annotation { "Feature Type Name" : "Feature", "Feature Type Description" : "" }
export const myFeature = defineFeature(function(context is Context, id is Id, definition is map)
    precondition{}
    {
        {
            var Q0;
            Q0=qCreatedBy(makeId("Top.planeOp"),FACE);
            var sketch = newSketch(context, id + "F0", { "sketchPlane" : qUnion([Q0])});
            skText(sketch, "E0", { "text": "RED ROBIN", "fontName": "OpenSans-Bold.ttf"});
            const initialGuessF0  = {"E0": [-0.07626, -0.00374, 1, 0, 0.02]};
            skSetInitialGuess(sketch, initialGuessF0);
            skSolve(sketch);
        }
        {
            var Q0;
            Q0 = qSketchRegion(id + "F0", true);
            extrude(context, id + "F1", {"entities" : qUnion([Q0]), "depth" : 3 * mm, "offsetDistance" : 25 * mm});
        }
        {
            var Q0;
            Q0=qCreatedBy(makeId("Top.planeOp"),FACE);
            var sketch = newSketch(context, id + "F2", { "sketchPlane" : qUnion([Q0])});
            skEllipse(sketch, "E1", {"center": v(0, 0) * mm, "majorRadius": 100 * mm, "minorRadius": 60 * mm, "majorAxis": v(1, 0)});
            skFitSpline(sketch, "E2.0", {"points": [v(94.93, -2.57) * mm, v(95.04, 0) * mm, v(94.93, 2.57) * mm, v(94.5, 5.97) * mm, v(93.46, 10.19) * mm, v(91.36, 15.2) * mm, v(88.41, 20.14) * mm, v(84.62, 24.96) * mm, v(80.76, 28.83) * mm, v(77.26, 31.82) * mm, v(74.43, 34) * mm, v(71.4, 36.11) * mm, v(68.17, 38.15) * mm, v(64.76, 40.1) * mm, v(61.2, 41.94) * mm, v(57.49, 43.68) * mm, v(52.36, 45.84) * mm, v(45.64, 48.25) * mm, v(37.12, 50.66) * mm, v(28.24, 52.57) * mm, v(20.58, 53.73) * mm, v(14.33, 54.39) * mm, v(9.6, 54.74) * mm, v(5.61, 54.92) * mm, v(2.41, 54.99) * mm, v(0, 55) * mm, v(-2.41, 54.99) * mm, v(-5.61, 54.92) * mm, v(-9.6, 54.74) * mm, v(-14.33, 54.39) * mm, v(-20.58, 53.73) * mm, v(-28.24, 52.57) * mm, v(-37.12, 50.66) * mm, v(-45.64, 48.25) * mm, v(-52.36, 45.84) * mm, v(-57.49, 43.68) * mm, v(-61.2, 41.94) * mm, v(-64.76, 40.1) * mm, v(-68.17, 38.15) * mm, v(-71.4, 36.11) * mm, v(-74.43, 34) * mm, v(-77.26, 31.82) * mm, v(-80.76, 28.83) * mm, v(-84.62, 24.96) * mm, v(-88.41, 20.14) * mm, v(-91.36, 15.2) * mm, v(-93.46, 10.19) * mm, v(-94.5, 5.97) * mm, v(-94.93, 2.57) * mm, v(-95.04, 0) * mm, v(-94.93, -2.57) * mm, v(-94.5, -5.97) * mm, v(-93.46, -10.19) * mm, v(-91.36, -15.2) * mm, v(-88.41, -20.14) * mm, v(-84.62, -24.96) * mm, v(-80.76, -28.83) * mm, v(-77.26, -31.82) * mm, v(-74.43, -34) * mm, v(-71.4, -36.11) * mm, v(-68.17, -38.15) * mm, v(-64.76, -40.1) * mm, v(-61.2, -41.94) * mm, v(-57.49, -43.68) * mm, v(-52.36, -45.84) * mm, v(-45.64, -48.25) * mm, v(-37.12, -50.66) * mm, v(-28.24, -52.57) * mm, v(-20.58, -53.73) * mm, v(-14.33, -54.39) * mm, v(-9.6, -54.74) * mm, v(-5.61, -54.92) * mm, v(-2.41, -54.99) * mm, v(0, -55) * mm, v(2.41, -54.99) * mm, v(5.61, -54.92) * mm, v(9.6, -54.74) * mm, v(14.33, -54.39) * mm, v(20.58, -53.73) * mm, v(28.24, -52.57) * mm, v(37.12, -50.66) * mm, v(45.64, -48.25) * mm, v(52.36, -45.84) * mm, v(57.49, -43.68) * mm, v(61.2, -41.94) * mm, v(64.76, -40.1) * mm, v(68.17, -38.15) * mm, v(71.4, -36.11) * mm, v(74.43, -34) * mm, v(77.26, -31.82) * mm, v(80.76, -28.83) * mm, v(84.62, -24.96) * mm, v(88.41, -20.14) * mm, v(91.36, -15.2) * mm, v(93.46, -10.19) * mm, v(94.5, -5.97) * mm, v(94.93, -2.57) * mm, v(95.04, 0) * mm, v(94.93, 2.57) * mm, v(94.93, -2.57) * mm]});
            skSolve(sketch);
        }
        {
            var Q0;
            Q0=makeQuery(id+"F2.imprint","IMPRINT",FACE,{"disambiguationData":[TD([[makeQuery(id+"F2.imprint","IMPRINT",EDGE,{"derivedFrom":sQuery(id+"F2.wireOp",EDGE,"E1")}),1.0]])]});
            extrude(context, id + "F3", {"entities" : qUnion([Q0]), "depth" : 3 * mm, "offsetDistance" : 25 * mm});
        }
        {
            var Q0;
            Q0=qCreatedBy(makeId("Top.planeOp"),FACE);
            var sketch = newSketch(context, id + "F4", { "sketchPlane" : qUnion([Q0])});
            skText(sketch, "E3", { "text": "8", "fontName": "OpenSans-Bold.ttf"});
            const initialGuessF4  = {"E3": [-0.00903, 0.02105, 1, 0, 0.03]};
            skSetInitialGuess(sketch, initialGuessF4);
            skSolve(sketch);
        }
        {
            var Q0;
            Q0=makeQuery(id+"F4.imprint","IMPRINT",FACE,{"disambiguationData":[TD([[makeQuery(id+"F4.imprint","IMPRINT",EDGE,{"derivedFrom":sQuery(id+"F4.wireOp",EDGE,"E3.sketch_text.stroke-0")}),-1.0]])]});
            extrude(context, id + "F5", {"entities" : qUnion([Q0]), "depth" : 3 * mm, "offsetDistance" : 25 * mm});
        }
        {
            var Q0;
            Q0=qCreatedBy(makeId("Top.planeOp"),FACE);
            var sketch = newSketch(context, id + "F6", { "sketchPlane" : qUnion([Q0])});
            skLineSegment(sketch, "E4", {"start": v(2.12, -51.56) * mm, "end": v(2.9, -50.82) * mm});
            skLineSegment(sketch, "E5", {"start": v(2.9, -50.82) * mm, "end": v(3.34, -50.14) * mm});
            skLineSegment(sketch, "E6", {"start": v(3.34, -50.14) * mm, "end": v(3.58, -49.42) * mm});
            skLineSegment(sketch, "E7", {"start": v(3.58, -49.42) * mm, "end": v(3.58, -48.63) * mm});
            skLineSegment(sketch, "E8", {"start": v(3.58, -48.63) * mm, "end": v(3.35, -47.95) * mm});
            skLineSegment(sketch, "E9", {"start": v(3.35, -47.95) * mm, "end": v(3.24, -47.49) * mm});
            skLineSegment(sketch, "E10", {"start": v(3.24, -47.49) * mm, "end": v(3.24, -47.15) * mm});
            skLineSegment(sketch, "E11", {"start": v(3.24, -47.15) * mm, "end": v(3.64, -47.33) * mm});
            skLineSegment(sketch, "E12", {"start": v(3.64, -47.33) * mm, "end": v(4.4, -47.66) * mm});
            skLineSegment(sketch, "E13", {"start": v(4.4, -47.66) * mm, "end": v(5.3, -48.2) * mm});
            skLineSegment(sketch, "E14", {"start": v(5.3, -48.2) * mm, "end": v(6.25, -48.75) * mm});
            skLineSegment(sketch, "E15", {"start": v(6.25, -48.75) * mm, "end": v(7.07, -49.26) * mm});
            skLineSegment(sketch, "E16", {"start": v(7.07, -49.26) * mm, "end": v(7.77, -49.77) * mm});
            skLineSegment(sketch, "E17", {"start": v(7.77, -49.77) * mm, "end": v(8.5, -50.3) * mm});
            skLineSegment(sketch, "E18", {"start": v(8.5, -50.3) * mm, "end": v(9.16, -50.81) * mm});
            skLineSegment(sketch, "E19", {"start": v(9.16, -50.81) * mm, "end": v(9.7, -51.21) * mm});
            skLineSegment(sketch, "E20", {"start": v(9.7, -51.21) * mm, "end": v(10.37, -51.78) * mm});
            skLineSegment(sketch, "E21", {"start": v(10.37, -51.78) * mm, "end": v(10.81, -52.24) * mm});
            skLineSegment(sketch, "E22", {"start": v(10.81, -52.24) * mm, "end": v(11.62, -51.83) * mm});
            skLineSegment(sketch, "E23", {"start": v(11.62, -51.83) * mm, "end": v(12.5, -51.3) * mm});
            skLineSegment(sketch, "E24", {"start": v(12.5, -51.3) * mm, "end": v(13.5, -50.63) * mm});
            skLineSegment(sketch, "E25", {"start": v(13.5, -50.63) * mm, "end": v(14.43, -49.99) * mm});
            skLineSegment(sketch, "E26", {"start": v(14.43, -49.99) * mm, "end": v(15.23, -49.34) * mm});
            skLineSegment(sketch, "E27", {"start": v(15.23, -49.34) * mm, "end": v(15.91, -48.73) * mm});
            skLineSegment(sketch, "E28", {"start": v(15.91, -48.73) * mm, "end": v(16.58, -48.1) * mm});
            skLineSegment(sketch, "E29", {"start": v(16.58, -48.1) * mm, "end": v(17.25, -47.42) * mm});
            skLineSegment(sketch, "E30", {"start": v(17.25, -47.42) * mm, "end": v(18.1, -46.54) * mm});
            skLineSegment(sketch, "E31", {"start": v(18.1, -46.54) * mm, "end": v(18.66, -45.75) * mm});
            skLineSegment(sketch, "E32", {"start": v(18.66, -45.75) * mm, "end": v(19.26, -44.88) * mm});
            skLineSegment(sketch, "E33", {"start": v(19.26, -44.88) * mm, "end": v(19.59, -44.47) * mm});
            skLineSegment(sketch, "E34", {"start": v(19.59, -44.47) * mm, "end": v(19.5, -44.22) * mm});
            skLineSegment(sketch, "E35", {"start": v(19.5, -44.22) * mm, "end": v(18.18, -43.77) * mm});
            skLineSegment(sketch, "E36", {"start": v(18.18, -43.77) * mm, "end": v(17.01, -43.42) * mm});
            skLineSegment(sketch, "E37", {"start": v(17.01, -43.42) * mm, "end": v(15.58, -42.98) * mm});
            skLineSegment(sketch, "E38", {"start": v(15.58, -42.98) * mm, "end": v(14.02, -42.6) * mm});
            skLineSegment(sketch, "E39", {"start": v(14.02, -42.6) * mm, "end": v(12.79, -42.3) * mm});
            skLineSegment(sketch, "E40", {"start": v(12.79, -42.3) * mm, "end": v(11.3, -41.98) * mm});
            skLineSegment(sketch, "E41", {"start": v(11.3, -41.98) * mm, "end": v(9.7, -41.67) * mm});
            skLineSegment(sketch, "E42", {"start": v(9.7, -41.67) * mm, "end": v(8.36, -41.46) * mm});
            skLineSegment(sketch, "E43", {"start": v(8.36, -41.46) * mm, "end": v(7.08, -41.32) * mm});
            skLineSegment(sketch, "E44", {"start": v(7.08, -41.32) * mm, "end": v(5.82, -41.21) * mm});
            skLineSegment(sketch, "E45", {"start": v(5.82, -41.21) * mm, "end": v(4.53, -41.05) * mm});
            skLineSegment(sketch, "E46", {"start": v(4.53, -41.05) * mm, "end": v(3.9, -40.9) * mm});
            skLineSegment(sketch, "E47", {"start": v(3.9, -40.9) * mm, "end": v(3.58, -40.77) * mm});
            skLineSegment(sketch, "E48", {"start": v(3.58, -40.77) * mm, "end": v(3.32, -40.45) * mm});
            skLineSegment(sketch, "E49", {"start": v(3.32, -40.45) * mm, "end": v(-3.26, -40.45) * mm});
            skLineSegment(sketch, "E50", {"start": v(-3.26, -40.45) * mm, "end": v(-3.36, -40.79) * mm});
            skLineSegment(sketch, "E51", {"start": v(-3.36, -40.79) * mm, "end": v(-3.5, -41.22) * mm});
            skLineSegment(sketch, "E52", {"start": v(-3.5, -41.22) * mm, "end": v(-3.5, -41.49) * mm});
            skLineSegment(sketch, "E53", {"start": v(-3.5, -41.49) * mm, "end": v(-3.5, -41.8) * mm});
            skLineSegment(sketch, "E54", {"start": v(-3.5, -41.8) * mm, "end": v(-3.33, -42.15) * mm});
            skLineSegment(sketch, "E55", {"start": v(-3.33, -42.15) * mm, "end": v(-3.2, -42.49) * mm});
            skLineSegment(sketch, "E56", {"start": v(-3.2, -42.49) * mm, "end": v(-3.13, -42.66) * mm});
            skLineSegment(sketch, "E57", {"start": v(-3.13, -42.66) * mm, "end": v(-3.13, -42.94) * mm});
            skLineSegment(sketch, "E58", {"start": v(-3.13, -42.94) * mm, "end": v(-3.3, -43.15) * mm});
            skLineSegment(sketch, "E59", {"start": v(-3.3, -43.15) * mm, "end": v(-3.36, -43.48) * mm});
            skLineSegment(sketch, "E60", {"start": v(-3.36, -43.48) * mm, "end": v(-3.36, -43.79) * mm});
            skLineSegment(sketch, "E61", {"start": v(-3.36, -43.79) * mm, "end": v(-3.25, -44.04) * mm});
            skLineSegment(sketch, "E62", {"start": v(-3.25, -44.04) * mm, "end": v(-3, -44.3) * mm});
            skLineSegment(sketch, "E63", {"start": v(-3, -44.3) * mm, "end": v(-2.8, -44.52) * mm});
            skLineSegment(sketch, "E64", {"start": v(-2.8, -44.52) * mm, "end": v(-2.67, -44.68) * mm});
            skLineSegment(sketch, "E65", {"start": v(-2.67, -44.68) * mm, "end": v(-2.67, -44.88) * mm});
            skLineSegment(sketch, "E66", {"start": v(-2.67, -44.88) * mm, "end": v(-2.64, -45.13) * mm});
            skLineSegment(sketch, "E67", {"start": v(-2.64, -45.13) * mm, "end": v(-2.8, -45.35) * mm});
            skLineSegment(sketch, "E68", {"start": v(-2.8, -45.35) * mm, "end": v(-2.86, -45.67) * mm});
            skLineSegment(sketch, "E69", {"start": v(-2.86, -45.67) * mm, "end": v(-2.93, -46.03) * mm});
            skLineSegment(sketch, "E70", {"start": v(-2.93, -46.03) * mm, "end": v(-2.77, -46.32) * mm});
            skLineSegment(sketch, "E71", {"start": v(-2.77, -46.32) * mm, "end": v(-2.53, -46.55) * mm});
            skLineSegment(sketch, "E72", {"start": v(-2.53, -46.55) * mm, "end": v(-2.24, -46.75) * mm});
            skLineSegment(sketch, "E73", {"start": v(-2.24, -46.75) * mm, "end": v(-2.14, -47.01) * mm});
            skLineSegment(sketch, "E74", {"start": v(-2.14, -47.01) * mm, "end": v(-2.14, -47.44) * mm});
            skLineSegment(sketch, "E75", {"start": v(-2.14, -47.44) * mm, "end": v(-2.3, -47.94) * mm});
            skLineSegment(sketch, "E76", {"start": v(-2.3, -47.94) * mm, "end": v(-2.48, -48.42) * mm});
            skLineSegment(sketch, "E77", {"start": v(-2.48, -48.42) * mm, "end": v(-2.56, -48.87) * mm});
            skLineSegment(sketch, "E78", {"start": v(-2.56, -48.87) * mm, "end": v(-2.56, -49.42) * mm});
            skLineSegment(sketch, "E79", {"start": v(-2.56, -49.42) * mm, "end": v(-2.36, -49.93) * mm});
            skLineSegment(sketch, "E80", {"start": v(-2.36, -49.93) * mm, "end": v(-2.07, -50.46) * mm});
            skLineSegment(sketch, "E81", {"start": v(-2.07, -50.46) * mm, "end": v(-1.75, -50.98) * mm});
            skLineSegment(sketch, "E82", {"start": v(-1.75, -50.98) * mm, "end": v(-1.33, -51.31) * mm});
            skLineSegment(sketch, "E83", {"start": v(-1.33, -51.31) * mm, "end": v(-0.93, -51.63) * mm});
            skLineSegment(sketch, "E84", {"start": v(-0.93, -51.63) * mm, "end": v(-0.48, -51.83) * mm});
            skLineSegment(sketch, "E85", {"start": v(-0.48, -51.83) * mm, "end": v(0.04, -51.92) * mm});
            skLineSegment(sketch, "E86", {"start": v(0.04, -51.92) * mm, "end": v(0.59, -52.02) * mm});
            skLineSegment(sketch, "E87", {"start": v(0.59, -52.02) * mm, "end": v(1.33, -51.92) * mm});
            skLineSegment(sketch, "E88", {"start": v(1.33, -51.92) * mm, "end": v(1.82, -51.72) * mm});
            skLineSegment(sketch, "E89", {"start": v(1.82, -51.72) * mm, "end": v(2.12, -51.56) * mm});
            skLineSegment(sketch, "E90", {"start": v(3.24, -37.87) * mm, "end": v(2.95, -16.1) * mm});
            skLineSegment(sketch, "E91", {"start": v(2.95, -16.1) * mm, "end": v(2.86, -14.7) * mm});
            skLineSegment(sketch, "E92", {"start": v(2.86, -14.7) * mm, "end": v(2.63, -13.64) * mm});
            skLineSegment(sketch, "E93", {"start": v(2.63, -13.64) * mm, "end": v(2.41, -12.84) * mm});
            skLineSegment(sketch, "E94", {"start": v(2.41, -12.84) * mm, "end": v(2.12, -11.93) * mm});
            skLineSegment(sketch, "E95", {"start": v(2.12, -11.93) * mm, "end": v(1.71, -11.08) * mm});
            skLineSegment(sketch, "E96", {"start": v(1.71, -11.08) * mm, "end": v(1.26, -10.27) * mm});
            skLineSegment(sketch, "E97", {"start": v(1.26, -10.27) * mm, "end": v(0.84, -9.62) * mm});
            skLineSegment(sketch, "E98", {"start": v(0.84, -9.62) * mm, "end": v(0.17, -8.65) * mm});
            skLineSegment(sketch, "E99", {"start": v(0.17, -8.65) * mm, "end": v(-0.4, -9.5) * mm});
            skLineSegment(sketch, "E100", {"start": v(-0.4, -9.5) * mm, "end": v(-0.76, -10.14) * mm});
            skLineSegment(sketch, "E101", {"start": v(-0.76, -10.14) * mm, "end": v(-1.07, -10.85) * mm});
            skLineSegment(sketch, "E102", {"start": v(-1.07, -10.85) * mm, "end": v(-1.5, -11.77) * mm});
            skLineSegment(sketch, "E103", {"start": v(-1.5, -11.77) * mm, "end": v(-1.74, -12.52) * mm});
            skLineSegment(sketch, "E104", {"start": v(-1.74, -12.52) * mm, "end": v(-1.88, -12.94) * mm});
            skLineSegment(sketch, "E105", {"start": v(-1.88, -12.94) * mm, "end": v(-1.96, -13.19) * mm});
            skLineSegment(sketch, "E106", {"start": v(-1.96, -13.19) * mm, "end": v(-2.1, -13.76) * mm});
            skLineSegment(sketch, "E107", {"start": v(-2.1, -13.76) * mm, "end": v(-2.19, -14.26) * mm});
            skLineSegment(sketch, "E108", {"start": v(-2.19, -14.26) * mm, "end": v(-2.28, -15.37) * mm});
            skLineSegment(sketch, "E109", {"start": v(-2.28, -15.37) * mm, "end": v(-2.77, -37.85) * mm});
            skLineSegment(sketch, "E110", {"start": v(-2.77, -37.85) * mm, "end": v(-2.77, -38.06) * mm});
            skLineSegment(sketch, "E111", {"start": v(-2.77, -38.06) * mm, "end": v(-5.75, -38.1) * mm});
            skLineSegment(sketch, "E112", {"start": v(-5.75, -38.1) * mm, "end": v(-6.37, -37.9) * mm});
            skLineSegment(sketch, "E113", {"start": v(-6.37, -37.9) * mm, "end": v(-6.86, -37.62) * mm});
            skLineSegment(sketch, "E114", {"start": v(-6.86, -37.62) * mm, "end": v(-7.23, -37.27) * mm});
            skLineSegment(sketch, "E115", {"start": v(-7.23, -37.27) * mm, "end": v(-7.49, -36.9) * mm});
            skLineSegment(sketch, "E116", {"start": v(-7.49, -36.9) * mm, "end": v(-7.66, -36.47) * mm});
            skLineSegment(sketch, "E117", {"start": v(-7.66, -36.47) * mm, "end": v(-7.8, -36.02) * mm});
            skLineSegment(sketch, "E118", {"start": v(-7.8, -36.02) * mm, "end": v(-8.05, -35.72) * mm});
            skLineSegment(sketch, "E119", {"start": v(-8.05, -35.72) * mm, "end": v(-8.4, -35.5) * mm});
            skLineSegment(sketch, "E120", {"start": v(-8.4, -35.5) * mm, "end": v(-8.9, -35.46) * mm});
            skLineSegment(sketch, "E121", {"start": v(-8.9, -35.46) * mm, "end": v(-9.35, -35.52) * mm});
            skLineSegment(sketch, "E122", {"start": v(-9.35, -35.52) * mm, "end": v(-9.65, -35.72) * mm});
            skLineSegment(sketch, "E123", {"start": v(-9.65, -35.72) * mm, "end": v(-9.9, -36.02) * mm});
            skLineSegment(sketch, "E124", {"start": v(-9.9, -36.02) * mm, "end": v(-10.07, -36.32) * mm});
            skLineSegment(sketch, "E125", {"start": v(-10.07, -36.32) * mm, "end": v(-10.17, -36.66) * mm});
            skLineSegment(sketch, "E126", {"start": v(-10.17, -36.66) * mm, "end": v(-10.22, -37.13) * mm});
            skLineSegment(sketch, "E127", {"start": v(-10.22, -37.13) * mm, "end": v(-10.21, -37.73) * mm});
            skLineSegment(sketch, "E128", {"start": v(-10.21, -37.73) * mm, "end": v(-10.14, -38.08) * mm});
            skLineSegment(sketch, "E129", {"start": v(-10.14, -38.08) * mm, "end": v(-9.97, -38.36) * mm});
            skLineSegment(sketch, "E130", {"start": v(-9.97, -38.36) * mm, "end": v(-9.78, -38.64) * mm});
            skLineSegment(sketch, "E131", {"start": v(-9.78, -38.64) * mm, "end": v(-9.53, -38.95) * mm});
            skLineSegment(sketch, "E132", {"start": v(-9.53, -38.95) * mm, "end": v(-9.24, -39.18) * mm});
            skLineSegment(sketch, "E133", {"start": v(-9.24, -39.18) * mm, "end": v(-8.88, -39.38) * mm});
            skLineSegment(sketch, "E134", {"start": v(-8.88, -39.38) * mm, "end": v(-8.5, -39.53) * mm});
            skLineSegment(sketch, "E135", {"start": v(-8.5, -39.53) * mm, "end": v(-7.88, -39.62) * mm});
            skLineSegment(sketch, "E136", {"start": v(-7.88, -39.62) * mm, "end": v(-7.1, -39.66) * mm});
            skLineSegment(sketch, "E137", {"start": v(-7.1, -39.66) * mm, "end": v(-5.9, -39.73) * mm});
            skLineSegment(sketch, "E138", {"start": v(-5.9, -39.73) * mm, "end": v(5.82, -39.62) * mm});
            skLineSegment(sketch, "E139", {"start": v(5.82, -39.62) * mm, "end": v(7.87, -39.73) * mm});
            skLineSegment(sketch, "E140", {"start": v(7.87, -39.73) * mm, "end": v(8.99, -39.93) * mm});
            skLineSegment(sketch, "E141", {"start": v(8.99, -39.93) * mm, "end": v(9.5, -40.13) * mm});
            skLineSegment(sketch, "E142", {"start": v(9.5, -40.13) * mm, "end": v(10.02, -40.38) * mm});
            skLineSegment(sketch, "E143", {"start": v(10.02, -40.38) * mm, "end": v(10.45, -40.67) * mm});
            skLineSegment(sketch, "E144", {"start": v(10.45, -40.67) * mm, "end": v(10.79, -40.9) * mm});
            skLineSegment(sketch, "E145", {"start": v(10.79, -40.9) * mm, "end": v(11.17, -41.1) * mm});
            skLineSegment(sketch, "E146", {"start": v(11.17, -41.1) * mm, "end": v(11.54, -41.24) * mm});
            skLineSegment(sketch, "E147", {"start": v(11.54, -41.24) * mm, "end": v(11.9, -41.3) * mm});
            skLineSegment(sketch, "E148", {"start": v(11.9, -41.3) * mm, "end": v(12.2, -41.2) * mm});
            skLineSegment(sketch, "E149", {"start": v(12.2, -41.2) * mm, "end": v(12.48, -41.01) * mm});
            skLineSegment(sketch, "E150", {"start": v(12.48, -41.01) * mm, "end": v(12.64, -40.79) * mm});
            skLineSegment(sketch, "E151", {"start": v(12.64, -40.79) * mm, "end": v(12.67, -40.32) * mm});
            skLineSegment(sketch, "E152", {"start": v(12.67, -40.32) * mm, "end": v(12.52, -39.96) * mm});
            skLineSegment(sketch, "E153", {"start": v(12.52, -39.96) * mm, "end": v(12.28, -39.52) * mm});
            skLineSegment(sketch, "E154", {"start": v(12.28, -39.52) * mm, "end": v(11.94, -39.15) * mm});
            skLineSegment(sketch, "E155", {"start": v(11.94, -39.15) * mm, "end": v(11.6, -38.9) * mm});
            skLineSegment(sketch, "E156", {"start": v(11.6, -38.9) * mm, "end": v(11.17, -38.7) * mm});
            skLineSegment(sketch, "E157", {"start": v(11.17, -38.7) * mm, "end": v(10.56, -38.46) * mm});
            skLineSegment(sketch, "E158", {"start": v(10.56, -38.46) * mm, "end": v(10.02, -38.3) * mm});
            skLineSegment(sketch, "E159", {"start": v(10.02, -38.3) * mm, "end": v(9.4, -38.14) * mm});
            skLineSegment(sketch, "E160", {"start": v(9.4, -38.14) * mm, "end": v(8.68, -38.07) * mm});
            skLineSegment(sketch, "E161", {"start": v(8.68, -38.07) * mm, "end": v(7.74, -37.97) * mm});
            skLineSegment(sketch, "E162", {"start": v(7.74, -37.97) * mm, "end": v(3.24, -37.97) * mm});
            skLineSegment(sketch, "E163", {"start": v(3.24, -37.97) * mm, "end": v(3.24, -37.87) * mm});
            skSolve(sketch);
        }
        {
            var Q0;
            Q0=makeQuery(id+"F6.imprint","IMPRINT",FACE,{"disambiguationData":[TD([[makeQuery(id+"F6.imprint","IMPRINT",EDGE,{"derivedFrom":sQuery(id+"F6.wireOp",EDGE,"E90")}),1.0]])]});
            var Q1;
            Q1=makeQuery(id+"F6.imprint","IMPRINT",FACE,{"disambiguationData":[TD([[makeQuery(id+"F6.imprint","IMPRINT",EDGE,{"derivedFrom":sQuery(id+"F6.wireOp",EDGE,"E4")}),1.0]])]});
            extrude(context, id + "F7", {"entities" : qUnion([Q0, Q1]), "depth" : 3 * mm, "offsetDistance" : 25 * mm});
        }
    });